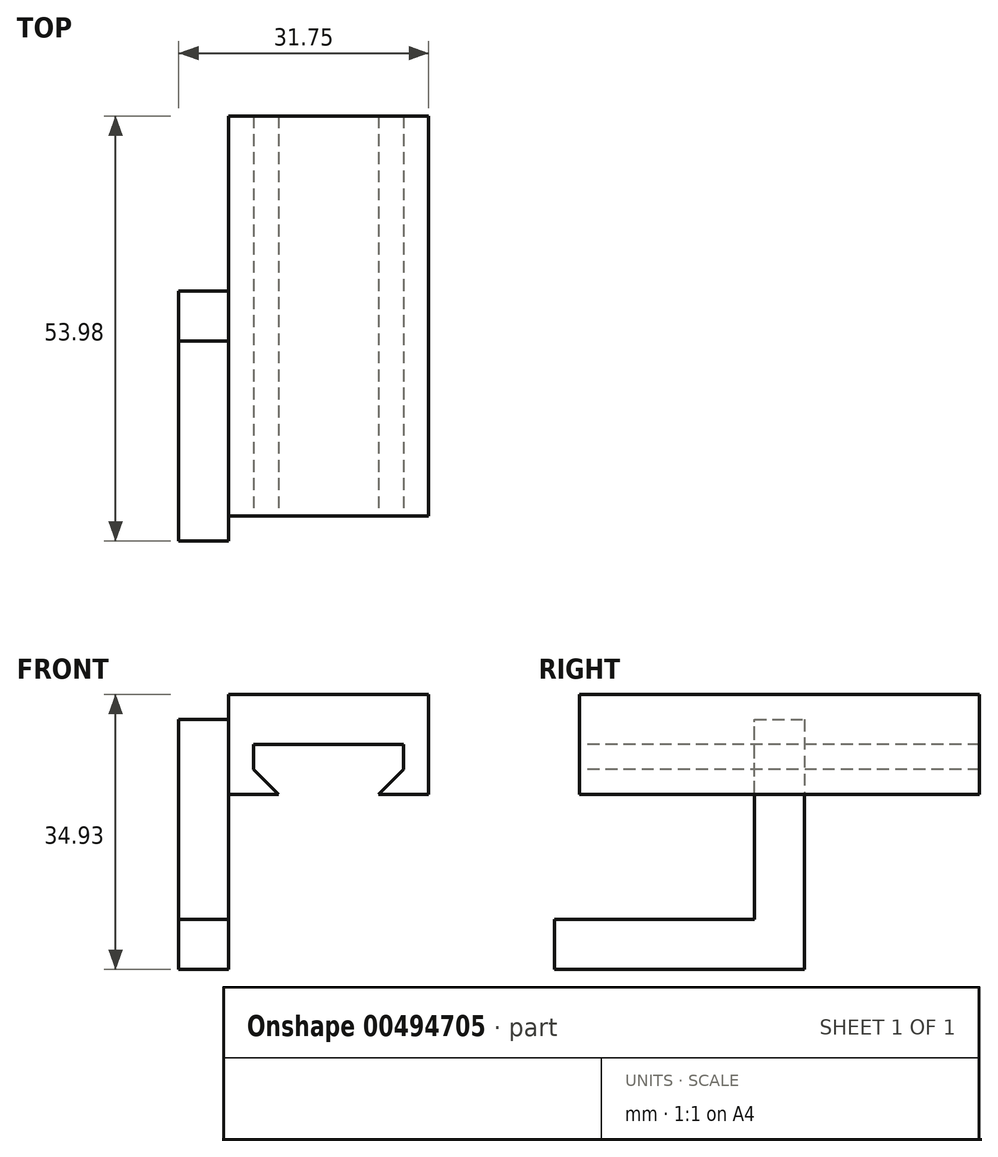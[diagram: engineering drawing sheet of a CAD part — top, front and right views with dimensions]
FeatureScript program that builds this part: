
annotation { "Feature Type Name" : "Feature", "Feature Type Description" : "" }
export const myFeature = defineFeature(function(context is Context, id is Id, definition is map)
    precondition{}
    {
        {
            var Q0;
            Q0=qCreatedBy(makeId("Front.planeOp"),FACE);
            var sketch = newSketch(context, id + "F0", { "sketchPlane" : qUnion([Q0])});
            skLineSegment(sketch, "E0", {"start": v(0, 0) * mm, "end": v(-6.35, 0) * mm});
            skLineSegment(sketch, "E1", {"start": v(-6.35, 0) * mm, "end": v(-12.7, 0) * mm});
            skLineSegment(sketch, "E2", {"start": v(-12.7, 0) * mm, "end": v(-12.7, 12.7) * mm});
            skLineSegment(sketch, "E3", {"start": v(-12.7, 12.7) * mm, "end": v(0, 12.7) * mm});
            skLineSegment(sketch, "E4", {"start": v(-6.35, 0) * mm, "end": v(-9.53, 3.17) * mm});
            skPoint(sketch, "E4.endSnap0", {"position": v(-9.53, 0) * mm});
            skLineSegment(sketch, "E5", {"start": v(-9.53, 3.17) * mm, "end": v(-9.53, 6.35) * mm});
            skLineSegment(sketch, "E6", {"start": v(-9.53, 6.35) * mm, "end": v(0, 6.35) * mm});
            skLineSegment(sketch, "E7.MirrorCS", {"start": v(9.53, 6.35) * mm, "end": v(0, 6.35) * mm});
            skLineSegment(sketch, "E8.MirrorCS", {"start": v(12.7, 12.7) * mm, "end": v(0, 12.7) * mm});
            skLineSegment(sketch, "E9.MirrorCS", {"start": v(12.7, 0) * mm, "end": v(12.7, 12.7) * mm});
            skLineSegment(sketch, "E10.MirrorCS", {"start": v(9.53, 3.17) * mm, "end": v(9.53, 6.35) * mm});
            skLineSegment(sketch, "E11.MirrorCS", {"start": v(6.35, 0) * mm, "end": v(9.53, 3.17) * mm});
            skLineSegment(sketch, "E12.MirrorCS", {"start": v(6.35, 0) * mm, "end": v(12.7, 0) * mm});
            skSolve(sketch);
        }
        {
            var Q0;
            Q0=makeQuery(id+"F0.imprint","IMPRINT",FACE,{"disambiguationData":[TD([[makeQuery(id+"F0.imprint","IMPRINT",EDGE,{"derivedFrom":sQuery(id+"F0.wireOp",EDGE,"E1")}),-1.0]])]});
            extrude(context, id + "F1", {"entities" : qUnion([Q0]), "oppositeDirection" : true, "depth" : 50.8 * mm});
        }
        {
            var Q0;
            Q0=makeQuery(id+"F1.opExtrude","SWEPT_FACE",FACE,{"disambiguationData":[OSD([sQuery(id+"F0.wireOp",EDGE,"E2")])]});
            var sketch = newSketch(context, id + "F2", { "sketchPlane" : qUnion([Q0])});
            skLineSegment(sketch, "E13", {"start": v(-50.8, 12.7) * mm, "end": v(-25.4, 12.7) * mm});
            skLineSegment(sketch, "E14", {"start": v(-25.4, 12.7) * mm, "end": v(-25.4, 6.35) * mm});
            skPoint(sketch, "E14.endSnap0", {"position": v(0, 6.35) * mm});
            skLineSegment(sketch, "E15", {"start": v(-25.4, 9.52) * mm, "end": v(-28.58, 9.52) * mm});
            skLineSegment(sketch, "E16", {"start": v(-28.58, 9.52) * mm, "end": v(-28.58, 3.17) * mm});
            skLineSegment(sketch, "E17", {"start": v(-28.58, 3.17) * mm, "end": v(-22.23, 3.17) * mm});
            skLineSegment(sketch, "E18", {"start": v(-22.23, 3.17) * mm, "end": v(-22.23, 9.53) * mm});
            skLineSegment(sketch, "E19", {"start": v(-22.23, 9.53) * mm, "end": v(-25.4, 9.52) * mm});
            skSolve(sketch);
        }
        {
            var Q0;
            Q0=makeQuery(id+"F2.imprint","IMPRINT",FACE,{"disambiguationData":[TD([[makeQuery(id+"F2.imprint","IMPRINT",EDGE,{"derivedFrom":sQuery(id+"F2.wireOp",EDGE,"E15")}),1.0]])]});
            extrude(context, id + "F3", {"entities" : qUnion([Q0]), "operationType" : NewBodyOperationType.ADD, "depth" : 6.35 * mm, "offsetDistance" : 25.4 * mm});
        }
        {
            var Q0;
            Q0=makeQuery(id+"F3.opExtrude","SWEPT_FACE",FACE,{"disambiguationData":[OSD([sQuery(id+"F2.wireOp",EDGE,"E17")])]});
            extrude(context, id + "F4", {"entities" : qUnion([Q0]), "operationType" : NewBodyOperationType.ADD, "depth" : 25.4 * mm, "offsetDistance" : 25.4 * mm});
        }
        {
            var Q0;
            {var subQ0=sQuery(id+"F2.wireOp",EDGE,"E18");Q0=makeQuery(id+"F4.boolean.opBoolean","MERGE",FACE,{"derivedFrom":[makeQuery(id+"F3.opExtrude","SWEPT_FACE",FACE,{"disambiguationData":[OSD([subQ0])]}),makeQuery(id+"F4.opExtrude","SWEPT_FACE",FACE,{"disambiguationData":[OSD([sQuery(id+"F2.wireOp",EDGE,"E17"),subQ0])]})]});}
            var sketch = newSketch(context, id + "F5", { "sketchPlane" : qUnion([Q0])});
            skLineSegment(sketch, "E20", {"start": v(-19.05, -22.23) * mm, "end": v(-19.05, -15.88) * mm});
            skLineSegment(sketch, "E21", {"start": v(-19.05, -15.88) * mm, "end": v(-12.7, -15.88) * mm});
            skLineSegment(sketch, "E22", {"start": v(-12.7, -15.88) * mm, "end": v(-12.7, -22.23) * mm});
            skLineSegment(sketch, "E23", {"start": v(-12.7, -22.23) * mm, "end": v(-19.05, -22.23) * mm});
            skSolve(sketch);
        }
        {
            var Q0;
            Q0=makeQuery(id+"F5.imprint","IMPRINT",FACE,{"disambiguationData":[TD([[makeQuery(id+"F5.imprint","IMPRINT",EDGE,{"derivedFrom":sQuery(id+"F5.wireOp",EDGE,"E20")}),-1.0]])]});
            extrude(context, id + "F6", {"entities" : qUnion([Q0]), "operationType" : NewBodyOperationType.ADD, "depth" : 25.4 * mm, "offsetDistance" : 25.4 * mm});
        }
    });
